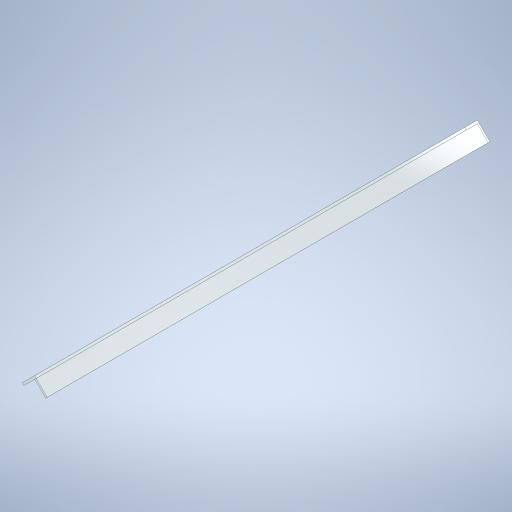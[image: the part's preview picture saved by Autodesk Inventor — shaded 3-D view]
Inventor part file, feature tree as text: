
AUTODESK INVENTOR PART (.ipt)
format: ipt  version: 2024 (Build 280153000, 153)  size: 263,680 bytes
history: native  units: in
note: dims shown in document units (in); Inventor stores cm internally (conversion verified against a paired STEP export)
features: extrude x1, sketch x1
ambient origin geometry x8: Origin, YZ Plane, XZ Plane, XY Plane, X Axis, Y Axis, Z Axis, Center Point
bodies: Solid1 (feature_tree)
feature tree (2):
  extrude  "Extrusion1"  Depth=12.0in
  sketch  "Sketch1"  dims[d0=1.5in d1=12.0in d2=300.0in d3=0.0in]
